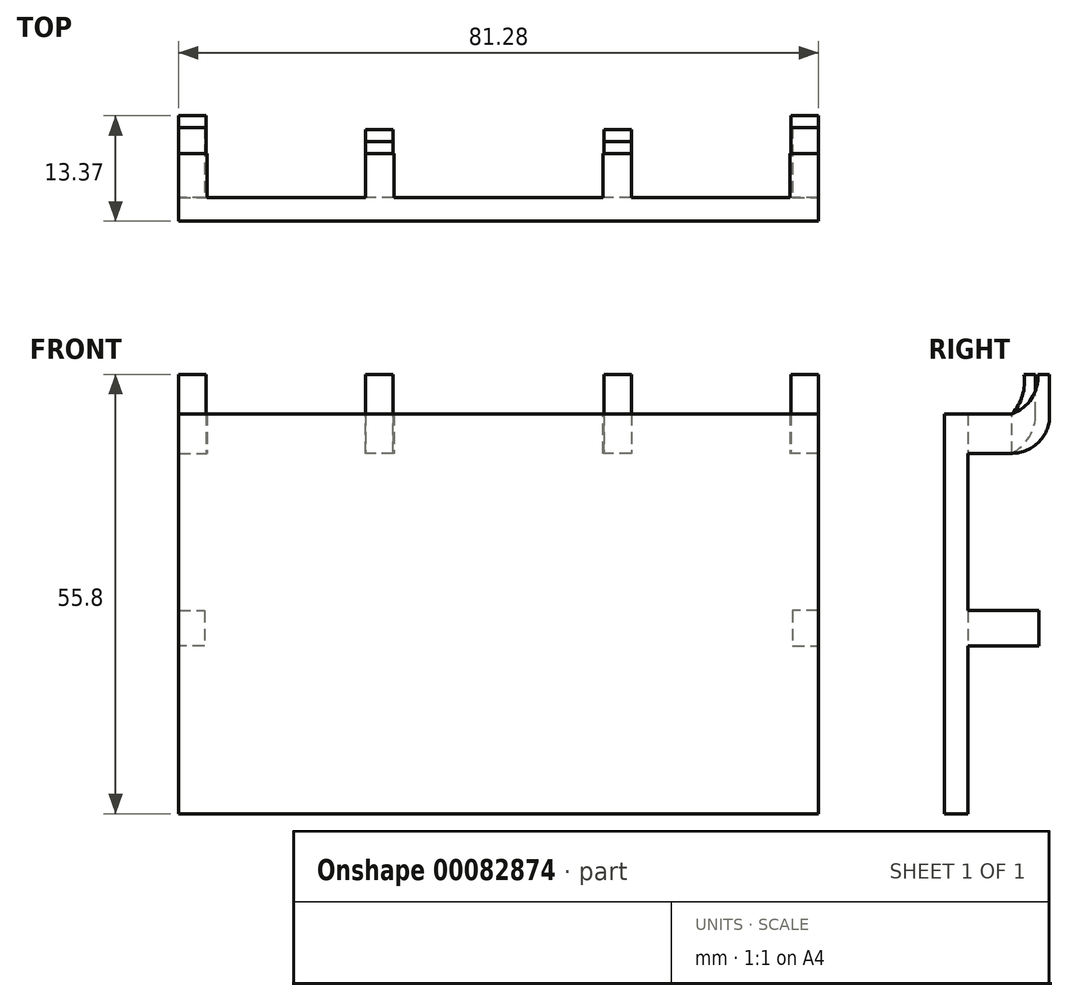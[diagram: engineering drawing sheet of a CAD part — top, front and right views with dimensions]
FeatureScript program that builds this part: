
annotation { "Feature Type Name" : "Feature", "Feature Type Description" : "" }
export const myFeature = defineFeature(function(context is Context, id is Id, definition is map)
    precondition{}
    {
        {
            var Q0;
            Q0=qCreatedBy(makeId("Front.planeOp"),FACE);
            var sketch = newSketch(context, id + "F0", { "sketchPlane" : qUnion([Q0])});
            skLineSegment(sketch, "E0.bottom", {"start": v(40.64, 25.4) * mm, "end": v(-40.64, 25.4) * mm});
            skLineSegment(sketch, "E0.top", {"start": v(40.64, -25.4) * mm, "end": v(-40.64, -25.4) * mm});
            skLineSegment(sketch, "E0.left", {"start": v(40.64, 25.4) * mm, "end": v(40.64, -25.4) * mm});
            skLineSegment(sketch, "E0.right", {"start": v(-40.64, 25.4) * mm, "end": v(-40.64, -25.4) * mm});
            skPoint(sketch, "E0.middle", {"position": v(0, 0) * mm});
            skSolve(sketch);
        }
        {
            var Q0;
            Q0=makeQuery(id+"F0.imprint","IMPRINT",FACE,{"disambiguationData":[TD([[makeQuery(id+"F0.imprint","IMPRINT",EDGE,{"derivedFrom":sQuery(id+"F0.wireOp",EDGE,"E0.bottom")}),1.0]])]});
            extrude(context, id + "F1", {"entities" : qUnion([Q0]), "depth" : 3 * mm});
        }
        {
            var Q0;
            Q0=makeQuery(id+"F1.opExtrude","CAP_FACE",FACE,{"disambiguationData":[OSD([sQuery(id+"F0.wireOp",EDGE,"E0.bottom"),sQuery(id+"F0.wireOp",EDGE,"E0.top"),sQuery(id+"F0.wireOp",EDGE,"E0.left"),sQuery(id+"F0.wireOp",EDGE,"E0.right")])],"isStart":true});
            var sketch = newSketch(context, id + "F2", { "sketchPlane" : qUnion([Q0])});
            skLineSegment(sketch, "E1.bottom", {"start": v(-40.64, 25.4) * mm, "end": v(-37.03, 25.4) * mm});
            skLineSegment(sketch, "E1.top", {"start": v(-40.64, 20.4) * mm, "end": v(-37.03, 20.4) * mm});
            skLineSegment(sketch, "E1.left", {"start": v(-40.64, 25.4) * mm, "end": v(-40.64, 20.4) * mm});
            skLineSegment(sketch, "E1.right", {"start": v(-37.03, 25.4) * mm, "end": v(-37.03, 20.4) * mm});
            skLineSegment(sketch, "E2.MirrorCS", {"start": v(37.03, 25.4) * mm, "end": v(37.03, 20.4) * mm});
            skLineSegment(sketch, "E3.MirrorCS", {"start": v(40.64, 25.4) * mm, "end": v(37.03, 25.4) * mm});
            skLineSegment(sketch, "E4.MirrorCS", {"start": v(40.64, 25.4) * mm, "end": v(40.64, 20.4) * mm});
            skLineSegment(sketch, "E5.MirrorCS", {"start": v(40.64, 20.4) * mm, "end": v(37.03, 20.4) * mm});
            skLineSegment(sketch, "E6", {"start": v(40.64, 20.4) * mm, "end": v(40.64, 0.4) * mm});
            skLineSegment(sketch, "E7", {"start": v(40.64, 0.4) * mm, "end": v(37.34, 0.4) * mm});
            skLineSegment(sketch, "E8", {"start": v(37.34, 0.4) * mm, "end": v(37.34, -4.09) * mm});
            skLineSegment(sketch, "E9", {"start": v(37.34, -4.09) * mm, "end": v(40.64, -4.09) * mm});
            skLineSegment(sketch, "E10", {"start": v(40.64, 0.4) * mm, "end": v(40.64, -4.09) * mm});
            skLineSegment(sketch, "E11.MirrorCS", {"start": v(-37.34, 0.4) * mm, "end": v(-37.34, -4.09) * mm});
            skLineSegment(sketch, "E12.MirrorCS", {"start": v(-37.34, -4.09) * mm, "end": v(-40.64, -4.09) * mm});
            skLineSegment(sketch, "E13.MirrorCS", {"start": v(-40.64, 0.4) * mm, "end": v(-40.64, -4.09) * mm});
            skLineSegment(sketch, "E14.MirrorCS", {"start": v(-40.64, 0.4) * mm, "end": v(-37.34, 0.4) * mm});
            skLineSegment(sketch, "E15", {"start": v(16.89, 25.4) * mm, "end": v(13.28, 25.4) * mm});
            skLineSegment(sketch, "E16", {"start": v(13.28, 25.4) * mm, "end": v(13.28, 20.4) * mm});
            skLineSegment(sketch, "E17", {"start": v(13.28, 20.4) * mm, "end": v(16.89, 20.4) * mm});
            skLineSegment(sketch, "E18", {"start": v(16.89, 20.4) * mm, "end": v(16.89, 25.4) * mm});
            skLineSegment(sketch, "E19", {"start": v(-37.03, 25.4) * mm, "end": v(-16.89, 25.4) * mm});
            skLineSegment(sketch, "E20", {"start": v(-16.89, 25.4) * mm, "end": v(-16.89, 20.4) * mm});
            skLineSegment(sketch, "E21", {"start": v(-16.89, 20.4) * mm, "end": v(-13.28, 20.4) * mm});
            skLineSegment(sketch, "E22", {"start": v(-13.28, 20.4) * mm, "end": v(-13.28, 25.4) * mm});
            skSolve(sketch);
        }
        {
            var Q0;
            Q0=makeQuery(id+"F2.imprint","IMPRINT",FACE,{"disambiguationData":[TD([[makeQuery(id+"F2.imprint","IMPRINT",EDGE,{"derivedFrom":sQuery(id+"F2.wireOp",EDGE,"E2.MirrorCS")}),1.0]])]});
            var Q1;
            Q1=makeQuery(id+"F2.imprint","IMPRINT",FACE,{"disambiguationData":[TD([[makeQuery(id+"F2.imprint","IMPRINT",EDGE,{"derivedFrom":sQuery(id+"F2.wireOp",EDGE,"E1.bottom")}),-1.0]])]});
            var Q2;
            {var subQ0=sQuery(id+"F2.wireOp",EDGE,"E20");Q2=makeQuery(id+"F2.imprint","IMPRINT",FACE,{"disambiguationData":[TD([[makeQuery(id+"F2.imprint","IMPRINT",EDGE,{"derivedFrom":subQ0}),1.0]])]});}
            var Q3;
            Q3=makeQuery(id+"F2.imprint","IMPRINT",FACE,{"disambiguationData":[TD([[makeQuery(id+"F2.imprint","IMPRINT",EDGE,{"derivedFrom":sQuery(id+"F2.wireOp",EDGE,"E15")}),-1.0]])]});
            extrude(context, id + "F3", {"entities" : qUnion([Q0, Q1, Q2, Q3]), "operationType" : NewBodyOperationType.ADD, "depth" : 5.6 * mm});
        }
        {
            var Q0;
            Q0=makeQuery(id+"F2.imprint","IMPRINT",FACE,{"disambiguationData":[TD([[makeQuery(id+"F2.imprint","IMPRINT",EDGE,{"derivedFrom":sQuery(id+"F2.wireOp",EDGE,"E11.MirrorCS")}),-1.0]])]});
            var Q1;
            Q1=makeQuery(id+"F2.imprint","IMPRINT",FACE,{"disambiguationData":[TD([[makeQuery(id+"F2.imprint","IMPRINT",EDGE,{"derivedFrom":sQuery(id+"F2.wireOp",EDGE,"E7")}),1.0]])]});
            extrude(context, id + "F4", {"entities" : qUnion([Q0, Q1]), "operationType" : NewBodyOperationType.ADD, "depth" : 9 * mm});
        }
        {
            var Q0;
            Q0=makeQuery(id+"F4.boolean.opBoolean","MERGE",FACE,{"derivedFrom":[makeQuery(id+"F3.boolean.opBoolean","MERGE",FACE,{"derivedFrom":[makeQuery(id+"F1.opExtrude","SWEPT_FACE",FACE,{"disambiguationData":[OSD([sQuery(id+"F0.wireOp",EDGE,"E0.right")])]}),makeQuery(id+"F3.opExtrude","SWEPT_FACE",FACE,{"disambiguationData":[OSD([sQuery(id+"F2.wireOp",EDGE,"E4.MirrorCS")])]})]}),makeQuery(id+"F4.opExtrude","SWEPT_FACE",FACE,{"disambiguationData":[OSD([sQuery(id+"F2.wireOp",EDGE,"E10")])]})]});
            var sketch = newSketch(context, id + "F5", { "sketchPlane" : qUnion([Q0])});
            skLineSegment(sketch, "E23", {"start": v(-10.36, 25.4) * mm, "end": v(-10.36, 30.4) * mm});
            skArc(sketch, "E24", {"start": v(-10.36, 25.4) * mm, "mid": v(-9.05, 21.88) * mm, "end": v(-5.59, 20.4) * mm});
            skLineSegment(sketch, "E25", {"start": v(-10.36, 30.4) * mm, "end": v(-8.86, 30.4) * mm});
            skArc(sketch, "E26", {"start": v(-8.86, 30.4) * mm, "mid": v(-8.07, 27.35) * mm, "end": v(-5.59, 25.4) * mm});
            skSolve(sketch);
        }
        {
            var Q0;
            Q0=makeQuery(id+"F5.imprint","IMPRINT",FACE,{"disambiguationData":[TD([[makeQuery(id+"F5.imprint","IMPRINT",EDGE,{"derivedFrom":sQuery(id+"F5.wireOp",EDGE,"E23")}),-1.0]])]});
            extrude(context, id + "F6", {"entities" : qUnion([Q0]), "operationType" : NewBodyOperationType.ADD, "oppositeDirection" : true, "depth" : 3.5 * mm});
        }
        {
            var Q0;
            Q0=makeQuery(id+"F1.opExtrude","SWEPT_BODY",BODY,{"disambiguationData":[OSD([sQuery(id+"F0.wireOp",EDGE,"E0.bottom"),sQuery(id+"F0.wireOp",EDGE,"E0.top"),sQuery(id+"F0.wireOp",EDGE,"E0.left"),sQuery(id+"F0.wireOp",EDGE,"E0.right")])]});
            var Q1;
            Q1=qCreatedBy(makeId("Right.planeOp"),FACE);
            mirror(context, id + "F7", {"operationType" : NewBodyOperationType.ADD, "entities" : qUnion([Q0]), "mirrorPlane" : qUnion([Q1])});
        }
        {
            var Q0;
            Q0=makeQuery(id+"F3.opExtrude","SWEPT_FACE",FACE,{"disambiguationData":[OSD([sQuery(id+"F2.wireOp",EDGE,"E18")])]});
            var sketch = newSketch(context, id + "F8", { "sketchPlane" : qUnion([Q0])});
            skLineSegment(sketch, "E27", {"start": v(-8.59, 25.4) * mm, "end": v(-8.59, 30.4) * mm});
            skLineSegment(sketch, "E28", {"start": v(-8.59, 30.4) * mm, "end": v(-7.09, 30.4) * mm});
            skArc(sketch, "E29", {"start": v(-8.59, 25.4) * mm, "mid": v(-7.78, 22.48) * mm, "end": v(-5.59, 20.4) * mm});
            skArc(sketch, "E30", {"start": v(-7.09, 30.4) * mm, "mid": v(-6.92, 27.73) * mm, "end": v(-5.59, 25.4) * mm});
            skSolve(sketch);
        }
        {
            var Q0;
            Q0 = qSketchRegion(id + "F8", true);
            var Q1;
            Q1=makeQuery(id+"F8.imprint","IMPRINT",FACE,{"disambiguationData":[TD([[makeQuery(id+"F8.imprint","IMPRINT",EDGE,{"derivedFrom":sQuery(id+"F8.wireOp",EDGE,"E27")}),-1.0]])]});
            extrude(context, id + "F9", {"entities" : qUnion([Q0, Q1]), "operationType" : NewBodyOperationType.ADD, "oppositeDirection" : true, "depth" : 3.5 * mm});
        }
        {
            var Q0;
            Q0=makeQuery(id+"F1.opExtrude","SWEPT_BODY",BODY,{"disambiguationData":[OSD([sQuery(id+"F0.wireOp",EDGE,"E0.bottom"),sQuery(id+"F0.wireOp",EDGE,"E0.top"),sQuery(id+"F0.wireOp",EDGE,"E0.left"),sQuery(id+"F0.wireOp",EDGE,"E0.right")])]});
            var Q1;
            Q1=qCreatedBy(makeId("Right.planeOp"),FACE);
            mirror(context, id + "F10", {"operationType" : NewBodyOperationType.ADD, "entities" : qUnion([Q0]), "mirrorPlane" : qUnion([Q1])});
        }
    });
